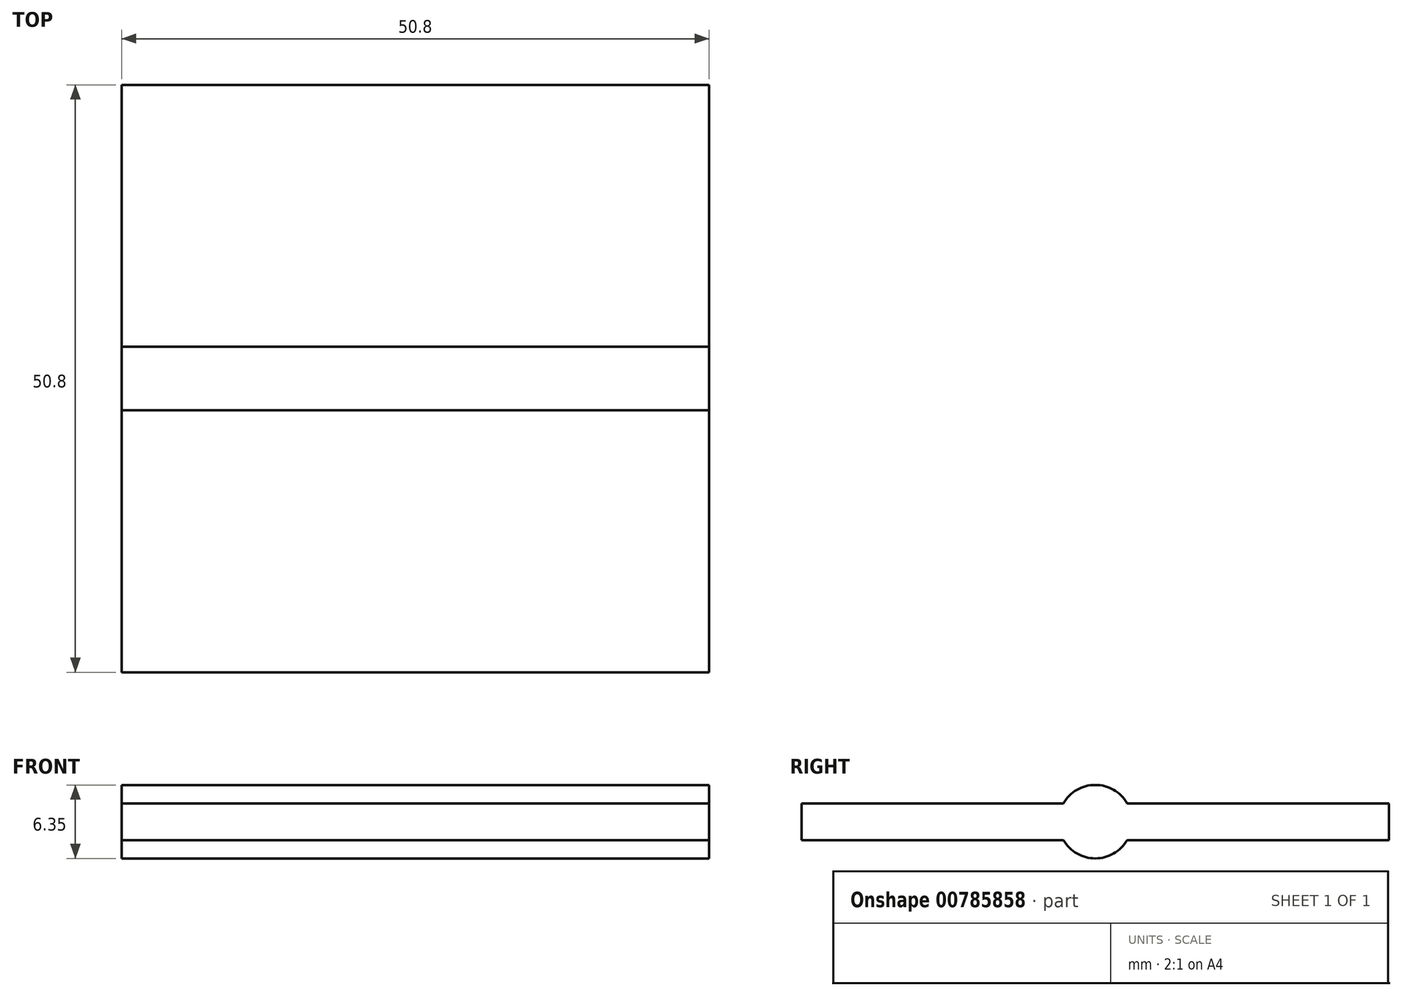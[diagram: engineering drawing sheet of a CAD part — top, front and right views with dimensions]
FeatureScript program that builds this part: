
annotation { "Feature Type Name" : "Feature", "Feature Type Description" : "" }
export const myFeature = defineFeature(function(context is Context, id is Id, definition is map)
    precondition{}
    {
        {
            var Q0;
            Q0=qCreatedBy(makeId("Top.planeOp"),FACE);
            var sketch = newSketch(context, id + "F0", { "sketchPlane" : qUnion([Q0])});
            skLineSegment(sketch, "E0.bottom", {"start": v(25.4, -25.4) * mm, "end": v(-25.4, -25.4) * mm});
            skLineSegment(sketch, "E0.top", {"start": v(25.4, 25.4) * mm, "end": v(-25.4, 25.4) * mm});
            skLineSegment(sketch, "E0.left", {"start": v(25.4, -25.4) * mm, "end": v(25.4, 25.4) * mm});
            skLineSegment(sketch, "E0.right", {"start": v(-25.4, -25.4) * mm, "end": v(-25.4, 25.4) * mm});
            skPoint(sketch, "E0.middle", {"position": v(0, 0) * mm});
            skSolve(sketch);
        }
        {
            var Q0;
            Q0 = qSketchRegion(id + "F0", true);
            extrude(context, id + "F1", {"entities" : qUnion([Q0]), "depth" : 3.17 * mm, "offsetDistance" : 25.4 * mm});
        }
        {
            var Q0;
            Q0=makeQuery(id+"F1.opExtrude","SWEPT_FACE",FACE,{"disambiguationData":[OSD([sQuery(id+"F0.wireOp",EDGE,"E0.right")])]});
            var sketch = newSketch(context, id + "F2", { "sketchPlane" : qUnion([Q0])});
            skCircle(sketch, "E1", {"center": v(0, 1.59) * mm, "radius": 3.18 * mm});
            skLineSegment(sketch, "E2", {"start": v(25.4, 1.59) * mm, "end": v(-25.4, 1.59) * mm, "construction": true});
            skSolve(sketch);
        }
        {
            var Q0;
            Q0 = qSketchRegion(id + "F2", true);
            var Q1;
            Q1=makeQuery(id+"F1.opExtrude","SWEPT_FACE",FACE,{"disambiguationData":[OSD([sQuery(id+"F0.wireOp",EDGE,"E0.left")])]});
            extrude(context, id + "F3", {"entities" : qUnion([Q0]), "operationType" : NewBodyOperationType.ADD, "endBound" : BoundingType.UP_TO_SURFACE, "oppositeDirection" : true, "depth" : 25.4 * mm, "endBoundEntityFace" : qUnion([Q1]), "offsetDistance" : 25.4 * mm});
        }
    });
